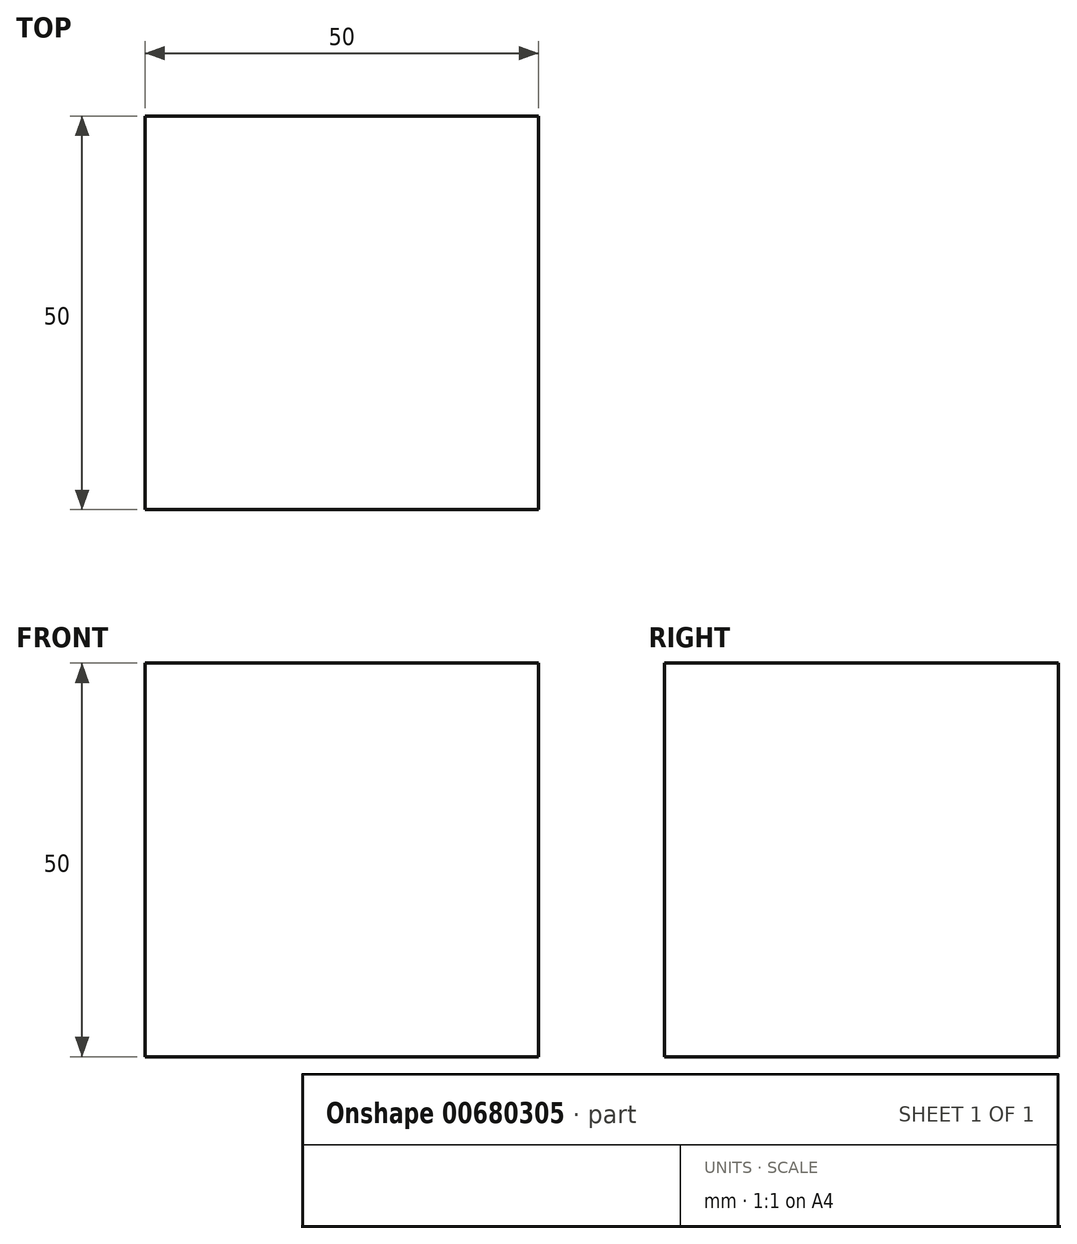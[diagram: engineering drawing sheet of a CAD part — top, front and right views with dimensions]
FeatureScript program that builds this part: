
annotation { "Feature Type Name" : "Feature", "Feature Type Description" : "" }
export const myFeature = defineFeature(function(context is Context, id is Id, definition is map)
    precondition{}
    {
        {
            var Q0;
            Q0=qCreatedBy(makeId("Top.planeOp"),FACE);
            var sketch = newSketch(context, id + "F0", { "sketchPlane" : qUnion([Q0])});
            skLineSegment(sketch, "E0.bottom", {"start": v(0, 0) * mm, "end": v(-50, 0) * mm});
            skLineSegment(sketch, "E0.top", {"start": v(0, -50) * mm, "end": v(-50, -50) * mm});
            skLineSegment(sketch, "E0.left", {"start": v(0, 0) * mm, "end": v(0, -50) * mm});
            skLineSegment(sketch, "E0.right", {"start": v(-50, 0) * mm, "end": v(-50, -50) * mm});
            skSolve(sketch);
        }
        {
            var Q0;
            Q0 = qSketchRegion(id + "F0", true);
            extrude(context, id + "F1", {"entities" : qUnion([Q0]), "depth" : 50 * mm, "offsetDistance" : 25 * mm});
        }
    });
